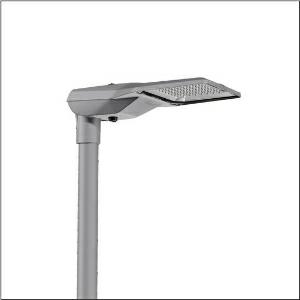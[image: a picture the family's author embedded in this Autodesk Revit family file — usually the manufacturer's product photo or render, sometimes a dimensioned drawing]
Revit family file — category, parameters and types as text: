
# Revit family: streetlight_sl_21_midi___st1_0a_5xe3d63t08lb_b124
name_source: partatom
category: Lighting Fixtures
units: mm (PartAtom-declared; Revit-internal decimal feet)

## family parameters
Cut with Voids When Loaded = No
Host = Face
Light Source = No
Part Type = Normal
Room Calculation Point = No
Round Connector Dimension = Use Diameter
Shared = No

## types (1)
- --- (1 x LED, 12860 lm, 99.6 W, 2700K)
    Apparent Load = 100 VA
    CIE Flux Codes = 37 72 97 100 100
    Color Rendering = 70
    Color Temperature = 2700K
    Default Elevation = 1800 mm
    Description = Streetlight SL 21 midi, mast luminaire, primary light control with lens, of PMMA, primary optical cover: cover, of toughened safety glass, transparent, light distribution: ST1.0a, light emission: direct distribution, primary light characteristic: asymmetric, installation type: side-entry, post-top, LED, High Power LED, rated luminous flux: 12.860lm, luminous efficacy: 129lm/W, light colour: 727, colour temperature: 2700K, control gear: D4i, control: overheat protection, constant luminous flux control, time-dependent luminous flux control, flexible luminous flux parameterisation, pre-setting: logarithmic dimming characteristic, mains connection: 230..240V, AC, 50/60Hz, start of lifetime: 100W, end of service life: 102W, reduction: 45W, luminaire housing, of diecast aluminium, powder-coated, Siteco® metallic grey (DB 702S), corrosivity category C5 mid according to DIN EN ISO 12944, please order mast flange separately, inclination adjustable: 0°, 5°, 10°, 15°, sealing non-destructively replaceable, multi-level sealing system, length: 644mm, width: 335mm, height: 110mm, mast flange for spigot size: 42mm (side-entry): 5XC10008XM4, 60/48mm (side-entry/post-top): 5XC10108XM2, 76/60mm (side-entry/post-top): 5XC10108XM1, mounting height: 4..8m, Smart Interface below and above, protection rating (complete): IP66, insulation class (complete): insulation class II (safety insulation), certification: CE, ENEC, ENEC+, VDE, impact resistance: IK10, permissible operating ambient temperature for outdoor applications: -40..+50°C, standard-compliant lighting for roads and squares, packaging unit: 1 piece

Light Distribution: ST1.0a
    Height = 111 mm
    Lamp = 1 x LED
    Lamp Light Flux = 12860 lm
    Lamp Power = 99.6 W
    Lamp count = 1
    Length = 644 mm
    Luminous efficacy = 129 lm/W
    Manufacturer = Siteco
    ModVariant = No
    Model = 5XE3D63T08LB
    Number of Poles = 1
    OnlyDefault = Yes
    Power Factor = 1
    Product Name = Streetlight SL 21 midi | ST1.0a
    Product group = mast luminaire | pylon top
    ProductGroupID = 6100
    Protection Class = Protection class II
    Protection Degree = IP 66
    RLX_Detail_Level = 1
    RLX_Emergency_Light_Flux = 0 lm
    RLX_Emergency_Type = 0
    RLX_Emergency_Type_DB = No
    RlxData = <blob elided: 26913 chars, md5=1d7dbe56>
    Socket = socket
    Standby Power = 0 W
    System Light Flux = 12860 lm
    System Power = 100 W
    Type Comments = factory setting: luminous flux: 100 % | dim-lin: 254 | 1020 mA
    Type Image = l_1004304.jpg
    URL = http://relux.com
    VarID = @adj_031971
    Voltage = 0 V
    Weight = 0.00 kg
    Width = 336 mm

## geometry (parser evidence)
native form markers: Blend x4, Sweep x12
no freeform markers — native parametric forms only
